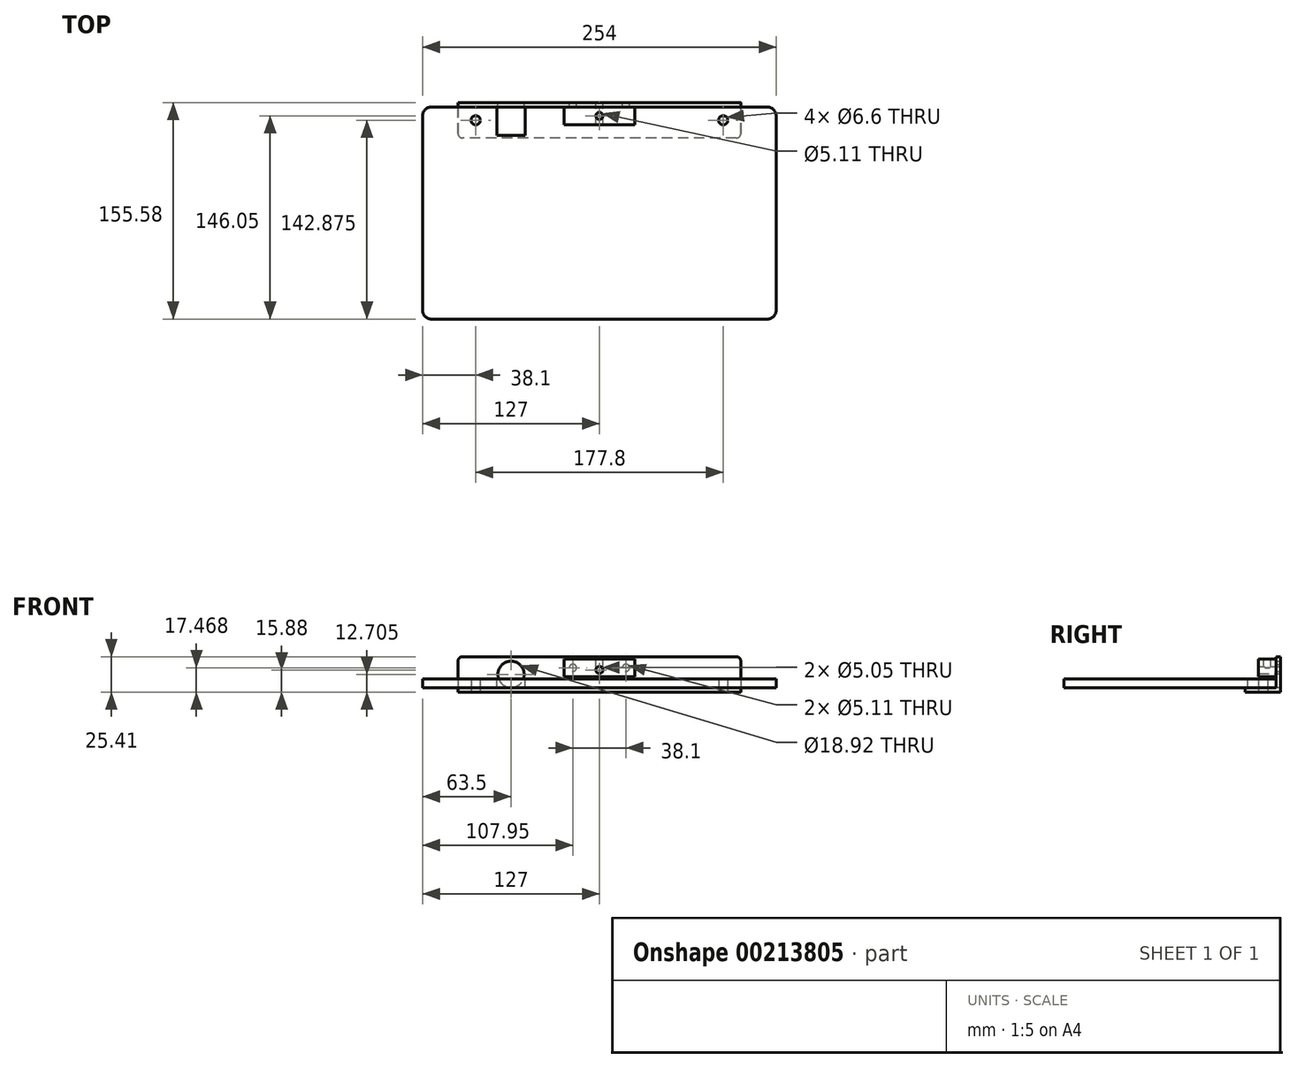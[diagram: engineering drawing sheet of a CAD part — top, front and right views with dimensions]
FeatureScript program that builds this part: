
annotation { "Feature Type Name" : "Feature", "Feature Type Description" : "" }
export const myFeature = defineFeature(function(context is Context, id is Id, definition is map)
    precondition{}
    {
        {
            var Q0;
            Q0=qCreatedBy(makeId("Top.planeOp"),FACE);
            var sketch = newSketch(context, id + "F0", { "sketchPlane" : qUnion([Q0])});
            skLineSegment(sketch, "E0.bottom", {"start": v(-120.65, 76.2) * mm, "end": v(120.65, 76.2) * mm});
            skLineSegment(sketch, "E0.top", {"start": v(-120.65, -76.2) * mm, "end": v(120.65, -76.2) * mm});
            skLineSegment(sketch, "E0.left", {"start": v(-127, 69.85) * mm, "end": v(-127, -69.85) * mm});
            skLineSegment(sketch, "E0.right", {"start": v(127, 69.85) * mm, "end": v(127, -69.85) * mm});
            skPoint(sketch, "E0.middle", {"position": v(0, 0) * mm});
            skPoint(sketch, "E1.visualSharp", {"position": v(-127, 76.2) * mm});
            skArc(sketch, "E1.filletArc", {"start": v(-120.65, 76.2) * mm, "mid": v(-125.14, 74.34) * mm, "end": v(-127, 69.85) * mm});
            skPoint(sketch, "E2.visualSharp", {"position": v(127, 76.2) * mm});
            skArc(sketch, "E2.filletArc", {"start": v(127, 69.85) * mm, "mid": v(125.14, 74.34) * mm, "end": v(120.65, 76.2) * mm});
            skPoint(sketch, "E3.visualSharp", {"position": v(127, -76.2) * mm});
            skArc(sketch, "E3.filletArc", {"start": v(120.65, -76.2) * mm, "mid": v(125.14, -74.34) * mm, "end": v(127, -69.85) * mm});
            skPoint(sketch, "E4.visualSharp", {"position": v(-127, -76.2) * mm});
            skArc(sketch, "E4.filletArc", {"start": v(-127, -69.85) * mm, "mid": v(-125.14, -74.34) * mm, "end": v(-120.65, -76.2) * mm});
            skSolve(sketch);
        }
        {
            var Q0;
            Q0=makeQuery(id+"F0.imprint","IMPRINT",FACE,{"disambiguationData":[TD([[makeQuery(id+"F0.imprint","IMPRINT",EDGE,{"derivedFrom":sQuery(id+"F0.wireOp",EDGE,"E0.bottom")}),-1.0]])]});
            extrude(context, id + "F1", {"entities" : qUnion([Q0]), "depth" : 6.35 * mm});
        }
        {
            var Q0;
            Q0=qCreatedBy(makeId("Right.planeOp"),FACE);
            var sketch = newSketch(context, id + "F2", { "sketchPlane" : qUnion([Q0])});
            skLineSegment(sketch, "E5", {"start": v(53.97, 0) * mm, "end": v(53.97, -3.18) * mm});
            skLineSegment(sketch, "E6", {"start": v(53.98, -3.18) * mm, "end": v(79.38, -3.17) * mm});
            skLineSegment(sketch, "E7", {"start": v(79.38, -3.17) * mm, "end": v(79.38, 22.23) * mm});
            skLineSegment(sketch, "E8", {"start": v(79.38, 22.23) * mm, "end": v(76.2, 22.23) * mm});
            skLineSegment(sketch, "E9", {"start": v(76.2, 22.23) * mm, "end": v(76.2, 0) * mm});
            skLineSegment(sketch, "E10", {"start": v(76.2, 0) * mm, "end": v(53.97, 0) * mm});
            skLineSegment(sketch, "E11.0", {"start": v(76.2, 6.35) * mm, "end": v(76.2, 0) * mm});
            skSolve(sketch);
        }
        {
            var Q0;
            Q0=makeQuery(id+"F2.imprint","IMPRINT",FACE,{"disambiguationData":[TD([[makeQuery(id+"F2.imprint","IMPRINT",EDGE,{"derivedFrom":sQuery(id+"F2.wireOp",EDGE,"E5")}),1.0]])]});
            extrude(context, id + "F3", {"entities" : qUnion([Q0]), "endBound" : BoundingType.SYMMETRIC, "depth" : 203.2 * mm});
        }
        {
            var Q0;
            Q0=makeQuery(id+"F3.opExtrude","CAP_EDGE",EDGE,{"disambiguationData":[OSD([sQuery(id+"F2.wireOp",EDGE,"E5")])],"isStart":true});
            var Q1;
            Q1=makeQuery(id+"F3.opExtrude","CAP_EDGE",EDGE,{"disambiguationData":[OSD([sQuery(id+"F2.wireOp",EDGE,"E5")])],"isStart":false});
            var Q2;
            Q2=makeQuery(id+"F3.opExtrude","CAP_EDGE",EDGE,{"disambiguationData":[OSD([sQuery(id+"F2.wireOp",EDGE,"E8")])],"isStart":false});
            var Q3;
            Q3=makeQuery(id+"F3.opExtrude","CAP_EDGE",EDGE,{"disambiguationData":[OSD([sQuery(id+"F2.wireOp",EDGE,"E8")])],"isStart":true});
            fillet(context, id + "F4", {"entities" : qUnion([Q0, Q1, Q2, Q3]), "radius" : 3.17 * mm, "tangentPropagation" : true, "allowEdgeOverflow" : false});
        }
        {
            var Q0;
            Q0=makeQuery(id+"F3.opExtrude","SWEPT_FACE",FACE,{"disambiguationData":[OSD([sQuery(id+"F2.wireOp",EDGE,"E6")])]});
            var sketch = newSketch(context, id + "F5", { "sketchPlane" : qUnion([Q0])});
            skPoint(sketch, "E12", {"position": v(-88.9, -66.67) * mm});
            skPoint(sketch, "E13", {"position": v(88.9, -66.67) * mm});
            skSolve(sketch);
        }
        {
            var Q0;
            Q0=sQuery(id+"F5.wireOp",VERTEX,"E12");
            var Q1;
            Q1=sQuery(id+"F5.wireOp",VERTEX,"E13");
            var Q2;
            Q2=makeQuery(id+"F1.opExtrude","SWEPT_BODY",BODY,{"disambiguationData":[OSD([sQuery(id+"F0.wireOp",EDGE,"E0.bottom"),sQuery(id+"F0.wireOp",EDGE,"E0.top"),sQuery(id+"F0.wireOp",EDGE,"E0.left"),sQuery(id+"F0.wireOp",EDGE,"E0.right"),sQuery(id+"F0.wireOp",EDGE,"E1.filletArc"),sQuery(id+"F0.wireOp",EDGE,"E2.filletArc"),sQuery(id+"F0.wireOp",EDGE,"E3.filletArc"),sQuery(id+"F0.wireOp",EDGE,"E4.filletArc")])]});
            var Q3;
            Q3=makeQuery(id+"F3.opExtrude","SWEPT_BODY",BODY,{"disambiguationData":[OSD([sQuery(id+"F2.wireOp",EDGE,"E5"),sQuery(id+"F2.wireOp",EDGE,"E6"),sQuery(id+"F2.wireOp",EDGE,"E7"),sQuery(id+"F2.wireOp",EDGE,"E8"),sQuery(id+"F2.wireOp",EDGE,"E9"),sQuery(id+"F2.wireOp",EDGE,"E10"),sQuery(id+"F2.wireOp",EDGE,"E11.0")])]});
            hole(context, id + "F6", {"style" : HoleStyle.SIMPLE, "endStyle" : HoleEndStyle.THROUGH, "holeDiameter" : 6.6 * mm, "tappedDepth" : 12.7 * mm, "tapClearance" : 3, "startFromSketch" : true, "locations" : qUnion([Q0, Q1]), "scope" : qUnion([Q2, Q3])});
        }
        {
            var Q0;
            Q0=makeQuery(id+"F3.opExtrude","SWEPT_FACE",FACE,{"disambiguationData":[OSD([sQuery(id+"F2.wireOp",EDGE,"E7")])]});
            var sketch = newSketch(context, id + "F7", { "sketchPlane" : qUnion([Q0])});
            skPoint(sketch, "E14", {"position": v(0, 12.7) * mm});
            skSolve(sketch);
        }
        {
            var Q0;
            Q0=sQuery(id+"F7.wireOp",VERTEX,"E14");
            var Q1;
            Q1=makeQuery(id+"F3.opExtrude","SWEPT_BODY",BODY,{"disambiguationData":[OSD([sQuery(id+"F2.wireOp",EDGE,"E5"),sQuery(id+"F2.wireOp",EDGE,"E6"),sQuery(id+"F2.wireOp",EDGE,"E7"),sQuery(id+"F2.wireOp",EDGE,"E8"),sQuery(id+"F2.wireOp",EDGE,"E9"),sQuery(id+"F2.wireOp",EDGE,"E10"),sQuery(id+"F2.wireOp",EDGE,"E11.0")])]});
            hole(context, id + "F8", {"style" : HoleStyle.SIMPLE, "endStyle" : HoleEndStyle.THROUGH, "holeDiameter" : 5.05 * mm, "tappedDepth" : 12.7 * mm, "tapClearance" : 3, "startFromSketch" : true, "locations" : qUnion([Q0]), "scope" : qUnion([Q1])});
        }
        {
            var Q0;
            Q0=makeQuery(id+"F3.opExtrude","SWEPT_FACE",FACE,{"disambiguationData":[OSD([sQuery(id+"F2.wireOp",EDGE,"E9"),sQuery(id+"F2.wireOp",EDGE,"E11.0")])]});
            var sketch = newSketch(context, id + "F9", { "sketchPlane" : qUnion([Q0])});
            skLineSegment(sketch, "E15.bottom", {"start": v(25.4, 7.94) * mm, "end": v(-25.4, 7.94) * mm});
            skLineSegment(sketch, "E15.top", {"start": v(25.4, 20.64) * mm, "end": v(-25.4, 20.64) * mm});
            skLineSegment(sketch, "E15.left", {"start": v(25.4, 7.94) * mm, "end": v(25.4, 20.64) * mm});
            skLineSegment(sketch, "E15.right", {"start": v(-25.4, 7.94) * mm, "end": v(-25.4, 20.64) * mm});
            skCircle(sketch, "E16.0", {"center": v(0, 12.7) * mm, "radius": 2.53 * mm});
            skSolve(sketch);
        }
        {
            var Q0;
            Q0=makeQuery(id+"F9.imprint","IMPRINT",FACE,{"disambiguationData":[TD([[makeQuery(id+"F9.imprint","IMPRINT",EDGE,{"derivedFrom":sQuery(id+"F9.wireOp",EDGE,"E15.bottom")}),-1.0]])]});
            extrude(context, id + "F10", {"entities" : qUnion([Q0]), "depth" : 12.7 * mm});
        }
        {
            var Q0;
            Q0=makeQuery(id+"F3.opExtrude","SWEPT_FACE",FACE,{"disambiguationData":[OSD([sQuery(id+"F2.wireOp",EDGE,"E7")])]});
            var sketch = newSketch(context, id + "F11", { "sketchPlane" : qUnion([Q0])});
            skPoint(sketch, "E17", {"position": v(19.05, 14.29) * mm});
            skPoint(sketch, "E18", {"position": v(-19.05, 14.29) * mm});
            skLineSegment(sketch, "E19.0", {"start": v(-25.4, 20.64) * mm, "end": v(25.4, 20.64) * mm});
            skLineSegment(sketch, "E20.0", {"start": v(-25.4, 7.94) * mm, "end": v(-25.4, 20.64) * mm});
            skCircle(sketch, "E21.0", {"center": v(0, 12.7) * mm, "radius": 2.53 * mm});
            skSolve(sketch);
        }
        {
            var Q0;
            Q0=sQuery(id+"F11.wireOp",VERTEX,"E18");
            var Q1;
            Q1=sQuery(id+"F11.wireOp",VERTEX,"E17");
            var Q2;
            Q2=makeQuery(id+"F3.opExtrude","SWEPT_BODY",BODY,{"disambiguationData":[OSD([sQuery(id+"F2.wireOp",EDGE,"E5"),sQuery(id+"F2.wireOp",EDGE,"E6"),sQuery(id+"F2.wireOp",EDGE,"E7"),sQuery(id+"F2.wireOp",EDGE,"E8"),sQuery(id+"F2.wireOp",EDGE,"E9"),sQuery(id+"F2.wireOp",EDGE,"E10"),sQuery(id+"F2.wireOp",EDGE,"E11.0")])]});
            hole(context, id + "F12", {"style" : HoleStyle.SIMPLE, "endStyle" : HoleEndStyle.THROUGH, "holeDiameter" : 5.1 * mm, "tappedDepth" : 12.7 * mm, "tapClearance" : 3, "startFromSketch" : true, "locations" : qUnion([Q0, Q1]), "scope" : qUnion([Q2])});
        }
        {
            var Q0;
            Q0=makeQuery(id+"F10.opExtrude","SWEPT_FACE",FACE,{"disambiguationData":[OSD([sQuery(id+"F9.wireOp",EDGE,"E15.top")])]});
            var sketch = newSketch(context, id + "F13", { "sketchPlane" : qUnion([Q0])});
            skPoint(sketch, "E22", {"position": v(0, 69.85) * mm});
            skSolve(sketch);
        }
        {
            var Q0;
            Q0=makeQuery(id+"F3.opExtrude","SWEPT_FACE",FACE,{"disambiguationData":[OSD([sQuery(id+"F2.wireOp",EDGE,"E7")])]});
            var sketch = newSketch(context, id + "F14", { "sketchPlane" : qUnion([Q0])});
            skPoint(sketch, "E23", {"position": v(63.5, 9.53) * mm});
            skCircle(sketch, "E24.0", {"center": v(0, 12.7) * mm, "radius": 2.53 * mm});
            skSolve(sketch);
        }
        {
            var Q0;
            Q0=sQuery(id+"F14.wireOp",VERTEX,"E23");
            var Q1;
            Q1=makeQuery(id+"F3.opExtrude","SWEPT_BODY",BODY,{"disambiguationData":[OSD([sQuery(id+"F2.wireOp",EDGE,"E5"),sQuery(id+"F2.wireOp",EDGE,"E6"),sQuery(id+"F2.wireOp",EDGE,"E7"),sQuery(id+"F2.wireOp",EDGE,"E8"),sQuery(id+"F2.wireOp",EDGE,"E9"),sQuery(id+"F2.wireOp",EDGE,"E10"),sQuery(id+"F2.wireOp",EDGE,"E11.0")])]});
            hole(context, id + "F15", {"style" : HoleStyle.SIMPLE, "endStyle" : HoleEndStyle.THROUGH, "holeDiameter" : 18.92 * mm, "tappedDepth" : 12.7 * mm, "tapClearance" : 3, "startFromSketch" : true, "locations" : qUnion([Q0]), "scope" : qUnion([Q1])});
        }
        {
            var Q0;
            Q0=sQuery(id+"F13.wireOp",VERTEX,"E22");
            var Q1;
            Q1=makeQuery(id+"F10.opExtrude","SWEPT_BODY",BODY,{"disambiguationData":[OSD([sQuery(id+"F9.wireOp",EDGE,"E15.bottom"),sQuery(id+"F9.wireOp",EDGE,"E15.top"),sQuery(id+"F9.wireOp",EDGE,"E15.left"),sQuery(id+"F9.wireOp",EDGE,"E15.right"),sQuery(id+"F9.wireOp",EDGE,"E16.0")])]});
            hole(context, id + "F16", {"style" : HoleStyle.SIMPLE, "endStyle" : HoleEndStyle.BLIND, "holeDiameter" : 5.1 * mm, "holeDepth" : 6.35 * mm, "tappedDepth" : 12.7 * mm, "tapClearance" : 3, "startFromSketch" : true, "locations" : qUnion([Q0]), "scope" : qUnion([Q1])});
        }
        {
            var Q0;
            Q0=makeQuery(id+"F1.opExtrude","CAP_FACE",FACE,{"disambiguationData":[OSD([sQuery(id+"F0.wireOp",EDGE,"E0.bottom"),sQuery(id+"F0.wireOp",EDGE,"E0.top"),sQuery(id+"F0.wireOp",EDGE,"E0.left"),sQuery(id+"F0.wireOp",EDGE,"E0.right"),sQuery(id+"F0.wireOp",EDGE,"E1.filletArc"),sQuery(id+"F0.wireOp",EDGE,"E2.filletArc"),sQuery(id+"F0.wireOp",EDGE,"E3.filletArc"),sQuery(id+"F0.wireOp",EDGE,"E4.filletArc")])],"isStart":false});
            var sketch = newSketch(context, id + "F17", { "sketchPlane" : qUnion([Q0])});
            skLineSegment(sketch, "E25.bottom", {"start": v(-73.66, 76.2) * mm, "end": v(-53.34, 76.2) * mm});
            skLineSegment(sketch, "E25.top", {"start": v(-73.66, 55.88) * mm, "end": v(-53.34, 55.88) * mm});
            skLineSegment(sketch, "E25.left", {"start": v(-73.66, 76.2) * mm, "end": v(-73.66, 55.88) * mm});
            skLineSegment(sketch, "E25.right", {"start": v(-53.34, 76.2) * mm, "end": v(-53.34, 55.88) * mm});
            skPoint(sketch, "E26", {"position": v(-63.5, 76.2) * mm});
            skCircle(sketch, "E27.0", {"center": v(0, 69.85) * mm, "radius": 2.55 * mm});
            skSolve(sketch);
        }
        {
            var Q0;
            Q0=makeQuery(id+"F17.imprint","IMPRINT",FACE,{"disambiguationData":[TD([[makeQuery(id+"F17.imprint","IMPRINT",EDGE,{"derivedFrom":sQuery(id+"F17.wireOp",EDGE,"E25.bottom")}),-1.0]])]});
            extrude(context, id + "F18", {"entities" : qUnion([Q0]), "operationType" : NewBodyOperationType.REMOVE, "endBound" : BoundingType.UP_TO_NEXT, "oppositeDirection" : true, "depth" : 25.4 * mm});
        }
    });
